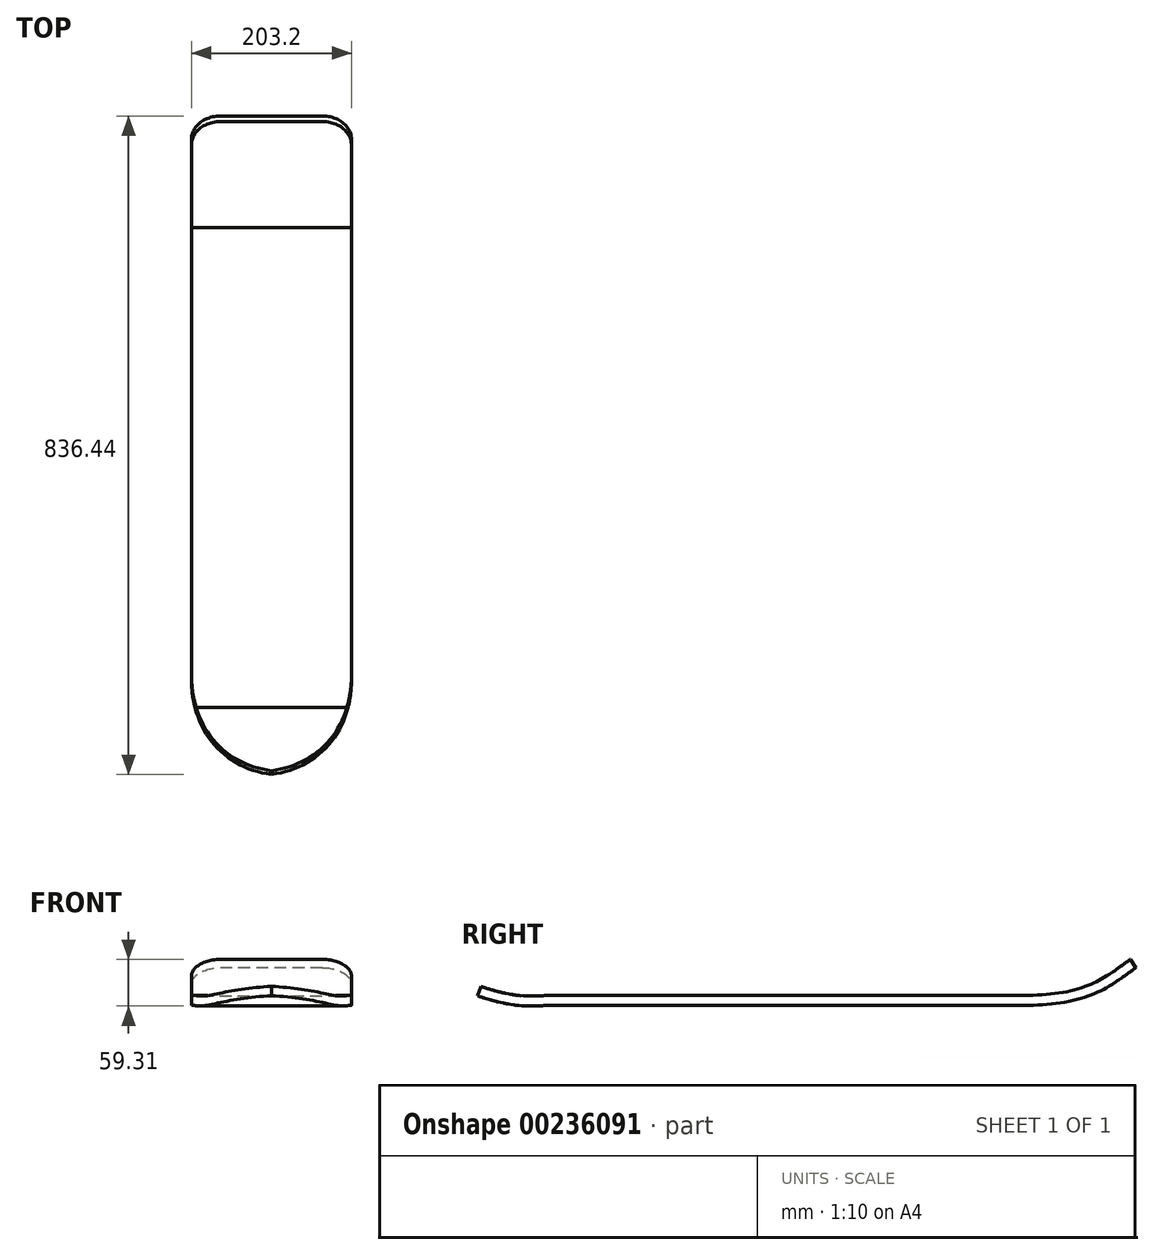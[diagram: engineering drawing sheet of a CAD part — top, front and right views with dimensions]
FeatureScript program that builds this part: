
annotation { "Feature Type Name" : "Feature", "Feature Type Description" : "" }
export const myFeature = defineFeature(function(context is Context, id is Id, definition is map)
    precondition{}
    {
        {
            var Q0;
            Q0=qCreatedBy(makeId("Top.planeOp"),FACE);
            var sketch = newSketch(context, id + "F0", { "sketchPlane" : qUnion([Q0])});
            skLineSegment(sketch, "E0.bottom", {"start": v(101.6, 304.8) * mm, "end": v(-101.6, 304.8) * mm});
            skLineSegment(sketch, "E0.top", {"start": v(101.6, -304.8) * mm, "end": v(-101.6, -304.8) * mm});
            skLineSegment(sketch, "E0.left", {"start": v(101.6, 304.8) * mm, "end": v(101.6, -304.8) * mm});
            skLineSegment(sketch, "E0.right", {"start": v(-101.6, 304.8) * mm, "end": v(-101.6, -304.8) * mm});
            skPoint(sketch, "E0.middle", {"position": v(0, 0) * mm});
            skSolve(sketch);
        }
        {
            var Q0;
            Q0=makeQuery(id+"F0.imprint","IMPRINT",FACE,{"disambiguationData":[TD([[makeQuery(id+"F0.imprint","IMPRINT",EDGE,{"derivedFrom":sQuery(id+"F0.wireOp",EDGE,"E0.bottom")}),1.0]])]});
            extrude(context, id + "F1", {"entities" : qUnion([Q0]), "endBound" : BoundingType.SYMMETRIC, "depth" : 12.7 * mm});
        }
        {
            var Q0;
            Q0=qCreatedBy(makeId("Right.planeOp"),FACE);
            var sketch = newSketch(context, id + "F2", { "sketchPlane" : qUnion([Q0])});
            skFitSpline(sketch, "E1", {"points": [v(304.93, 0) * mm, v(355.6, 4.2) * mm, v(391.76, 14.87) * mm, v(414.28, 26.73) * mm, v(443.32, 47.17) * mm], "startDerivative": vector(177.94, 7.03) * mm, "endDerivative": vector(123.05, 90.23) * mm});
            skFitSpline(sketch, "E2", {"points": [v(-304.6, 0) * mm, v(-336.38, 0) * mm, v(-369.62, 6.53) * mm, v(-388.25, 12.37) * mm], "startDerivative": vector(-87.41, -4.48) * mm, "endDerivative": vector(-61.36, 20.7) * mm});
            skSolve(sketch);
        }
        {
            var Q0;
            Q0=makeQuery(id+"F1.opExtrude","SWEPT_FACE",FACE,{"disambiguationData":[OSD([sQuery(id+"F0.wireOp",EDGE,"E0.bottom")])]});
            var Q1;
            Q1=sQuery(id+"F2.wireOp",EDGE,"E1");
            sweep(context, id + "F3", {"operationType" : NewBodyOperationType.ADD, "profiles" : qUnion([Q0]), "path" : qUnion([Q1])});
        }
        {
            var Q0;
            Q0=makeQuery(id+"F1.opExtrude","SWEPT_FACE",FACE,{"disambiguationData":[OSD([sQuery(id+"F0.wireOp",EDGE,"E0.top")])]});
            var Q1;
            Q1=sQuery(id+"F2.wireOp",EDGE,"E2");
            sweep(context, id + "F4", {"operationType" : NewBodyOperationType.ADD, "profiles" : qUnion([Q0]), "path" : qUnion([Q1])});
        }
        {
            var Q0;
            Q0=makeQuery(id+"F4.opSweep","CAP_EDGE",EDGE,{"disambiguationData":[OSD([sQuery(id+"F0.wireOp",EDGE,"E0.top"),sQuery(id+"F0.wireOp",EDGE,"E0.right"),sQuery(id+"F2.wireOp",VERTEX,"E2.end")])],"isStart":false});
            var Q1;
            Q1=makeQuery(id+"F4.opSweep","CAP_EDGE",EDGE,{"disambiguationData":[OSD([sQuery(id+"F0.wireOp",EDGE,"E0.top"),sQuery(id+"F0.wireOp",EDGE,"E0.left"),sQuery(id+"F2.wireOp",VERTEX,"E2.end")])],"isStart":false});
            fillet(context, id + "F5", {"entities" : qUnion([Q0, Q1]), "radius" : 116.5 * mm, "tangentPropagation" : true, "allowEdgeOverflow" : false});
        }
        {
            var Q0;
            Q0=makeQuery(id+"F3.opSweep","CAP_EDGE",EDGE,{"disambiguationData":[OSD([sQuery(id+"F0.wireOp",EDGE,"E0.bottom"),sQuery(id+"F0.wireOp",EDGE,"E0.left"),sQuery(id+"F2.wireOp",VERTEX,"E1.end")])],"isStart":false});
            var Q1;
            Q1=makeQuery(id+"F3.opSweep","CAP_EDGE",EDGE,{"disambiguationData":[OSD([sQuery(id+"F0.wireOp",EDGE,"E0.bottom"),sQuery(id+"F0.wireOp",EDGE,"E0.right"),sQuery(id+"F2.wireOp",VERTEX,"E1.end")])],"isStart":false});
            fillet(context, id + "F6", {"entities" : qUnion([Q0, Q1]), "radius" : 36.8 * mm, "tangentPropagation" : true, "allowEdgeOverflow" : false});
        }
    });
